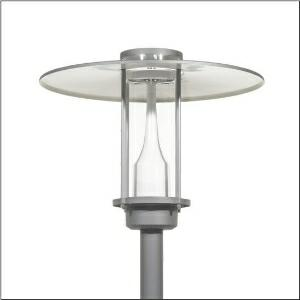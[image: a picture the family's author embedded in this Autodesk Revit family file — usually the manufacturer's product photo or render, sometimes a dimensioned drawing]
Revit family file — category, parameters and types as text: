
# Revit family: city-light_plus_iq___st1_2a_5xa5275kf14h_242a
name_source: partatom
category: Lighting Fixtures
units: mm (PartAtom-declared; Revit-internal decimal feet)

## family parameters
Cut with Voids When Loaded = No
Host = Face
Light Source = No
Part Type = Normal
Room Calculation Point = No
Round Connector Dimension = Use Diameter
Shared = No

## types (1)
- --- (1 x LED, 1470 lm, 10 W, 4000K)
    Apparent Load = 10 VA
    CIE Flux Codes = 22 62 93 97 100
    Color Rendering = 70
    Color Temperature = 4000K
    Default Elevation = 1800 mm
    Description = City-Light Plus iQ, mast luminaire, Module 540 iQ-SR, primary light control with 3 zone facetted reflector, of plastic, silver coated, highly specular, structured, primary optical cover: cover, of PMMA, transparent, light distribution: ST1.2a, light emission: direct distribution, primary light characteristic: asymmetric, installation type: post-top, LED, High Power LED, rated luminous flux: 1.470lm, luminous efficacy: 147lm/W, light colour: 740, colour temperature: 4000K, control gear: iQ Street-Remote, control: pre-setting: logarithmic dimming characteristic, Street-Remote, Auto-Match, Temp-Guard, Lumen-Switch, Night-Set, Smart-Wire, Light-Fading, Desk-Remote (wireless, voltage-free reading and setting of iQ features in the workshop via application-optimized NFC function/RFID function), optimised constant luminous flux control (CLO 2.0), with terminal, 6-pole, max. 2.5mm², mains connection: 230..240V, AC, 50/60Hz, start of lifetime: 10W, end of service life: 10W, reduction: 5W, luminaire housing, upper part, of glass-fibre reinforced polyester, coated, Siteco® metallic grey (DB 702S), diameter: 750mm, height: 590mm, spigot size: d x l = 76 x 70mm (post-top) | with reducer (optional accessory) 60 x 70mm, mounting height: 3..5m, post-top mast mounting element, of diecast aluminium, coated, Siteco® metallic grey (DB 702S), Module 540 iQ-SR, traffic white (RAL 9016), equipment: standard, protection rating (complete): IP65, insulation class (complete): insulation class II (safety insulation), certification: CE, ENEC, VDE, packaging unit: 1 piece

Light Distribution: ST1.2a
    Height = 590 mm
    Lamp = 1 x LED
    Lamp Light Flux = 1470 lm
    Lamp Power = 10 W
    Lamp count = 1
    Length = 750 mm
    Luminous efficacy = 147 lm/W
    Manufacturer = Siteco
    ModVariant = No
    Model = 5XA5275KF14H
    Number of Poles = 1
    OnlyDefault = Yes
    Power Factor = 1
    Product Name = City-Light Plus iQ | ST1.2a
    Product group = mast luminaire | pylon top
    ProductGroupID = 6100
    Protection Class = Protection class II
    Protection Degree = IP 65
    RLX_Detail_Level = 1
    RLX_Emergency_Light_Flux = 0 lm
    RLX_Emergency_Type = 0
    RLX_Emergency_Type_DB = No
    RlxData = <blob elided: 100009 chars, md5=53fc352c>
    Socket = socket
    Standby Power = 0 W
    System Light Flux = 1470 lm
    System Power = 10 W
    Type Comments = factory setting: luminous flux: 100 % | dim-lin: 254 | 401 mA
    Type Image = l_1006456.jpg
    URL = http://relux.com
    VarID = @adj_181549
    Voltage = 0 V
    Weight = 0.00 kg
    Width = 0 mm  [stored 0 ft]

note: [stored X ft] marks values corroborated as IEEE doubles in the binary element streams (Revit-internal decimal feet)

## geometry (parser evidence)
native form markers: Blend x4, Sweep x11
no freeform markers — native parametric forms only
